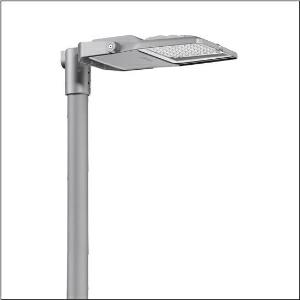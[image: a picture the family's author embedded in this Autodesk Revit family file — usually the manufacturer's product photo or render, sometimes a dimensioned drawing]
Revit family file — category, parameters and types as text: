
# Revit family: floodlight_fl_21_mini___pl43_5xa7775d2a3a_0001
name_source: partatom
category: Lighting Fixtures
units: mm (PartAtom-declared; Revit-internal decimal feet)

## family parameters
Cut with Voids When Loaded = No
Host = Face
Light Source = No
Part Type = Normal
Room Calculation Point = No
Round Connector Dimension = Use Diameter
Shared = No

## types (1)
- --- (1 x LED, 18300 lm, 142.9 W, 3000K)
    Apparent Load = 143 VA
    CIE Flux Codes = 27 78 99 100 100
    Color Rendering = 70
    Color Temperature = 3000K
    Default Elevation = 1800 mm
    Description = Floodlight FL 21 mini, floodlight, primary light control with lens, of PMMA, primary optical cover: protective disc, of toughened safety glass, transparent, light distribution: PL43, light emission: direct distribution, installation type: surface-mounted, LED, High Power LED, rated luminous flux: 18.300lm, luminous efficacy: 128lm/W, light colour: 730, colour temperature: 3000K, control: flexible luminous flux parameterisation, time-dependent luminous flux control, constant luminous flux control, overheat protection, pre-setting: logarithmic dimming characteristic, with terminal, 6-pole, mains connection: 220..240V, AC, 50/60Hz, start of lifetime: 143W, end of service life: 151W, reduction: 63W, luminaire housing, of diecast aluminium, powder-coated, Siteco® metallic grey (DB 702S), corrosivity category C5 mid according to DIN EN ISO 12944, sealing non-destructively replaceable, please order mast flange separately, mast bracket, of steel, galvanised, powder-coated, Siteco® metallic grey (DB 702S), Smart Interface above, protection rating (complete): IP66, insulation class (complete): insulation class II (safety insulation), certification: CE, ENEC, VDE, protection symbol: D, impact resistance: IK08, permissible operating ambient temperature: -40..+40°C, permissible operating ambient temperature for outdoor applications: -40..+50°C, standard: DIN EN 12944, LABS conformity tested according to VDMA 24364:2018-05, packaging unit: 1 piece

Light Distribution: PL43
    Height = 70 mm
    Lamp = 1 x LED
    Lamp Light Flux = 18300 lm
    Lamp Power = 142.9 W
    Lamp count = 1
    Length = 485 mm
    Luminous efficacy = 128 lm/W
    Manufacturer = Siteco
    ModVariant = No
    Model = 5XA7775D2A3A
    Number of Poles = 1
    OnlyDefault = Yes
    Power Factor = 1
    Product Name = Floodlight FL 21 mini | PL43
    Product group = floodlight | pylon annexe
    ProductGroupID = 6200
    Protection Class = Protection class II
    Protection Degree = IP 66
    RLX_Detail_Level = 1
    RLX_Emergency_Light_Flux = 0 lm
    RLX_Emergency_Type = 0
    RLX_Emergency_Type_DB = No
    RlxData = <blob elided: 101169 chars, md5=57763755>
    Socket = socket
    Standby Power = 0 W
    System Light Flux = 18300 lm
    System Power = 143 W
    Type Comments = factory setting: luminous flux: 100 % | dim-lin: 254 | 730 mA
    Type Image = l_1007125.jpg
    URL = http://relux.com
    VarID = @adj_131321
    Voltage = 0 V
    Weight = 0.00 kg
    Width = 337 mm

## geometry (parser evidence)
native form markers: Blend x4, Sweep x14
no freeform markers — native parametric forms only
